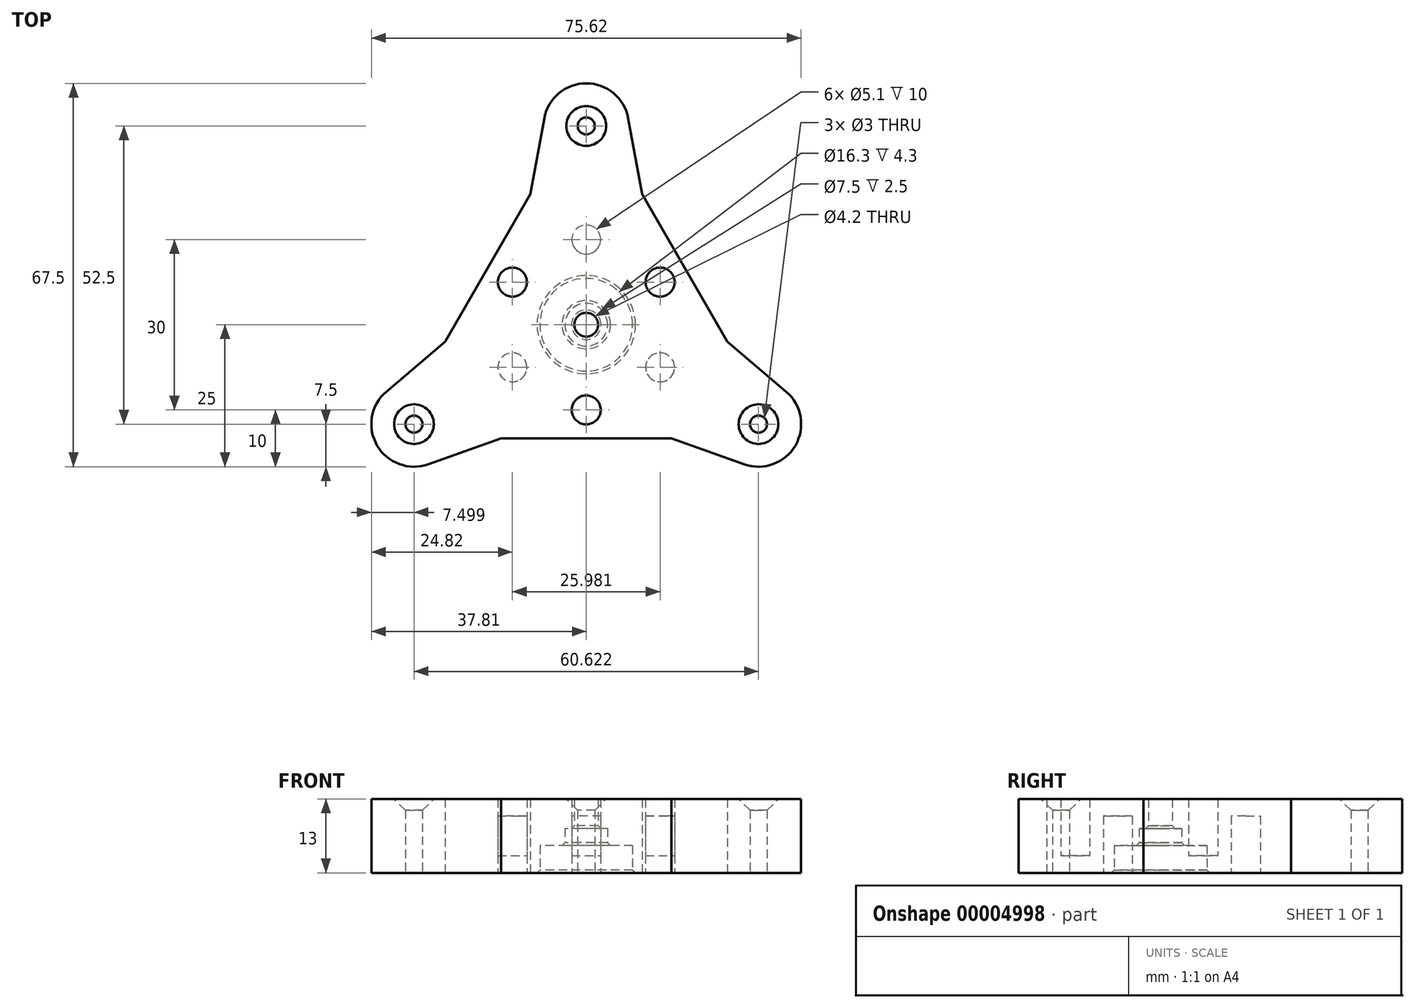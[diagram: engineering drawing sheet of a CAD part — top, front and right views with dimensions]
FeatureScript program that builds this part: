
annotation { "Feature Type Name" : "Feature", "Feature Type Description" : "" }
export const myFeature = defineFeature(function(context is Context, id is Id, definition is map)
    precondition{}
    {
        {
            var Q0;
            Q0=qCreatedBy(makeId("Top.planeOp"),FACE);
            var sketch = newSketch(context, id + "F0", { "sketchPlane" : qUnion([Q0])});
            skCircle(sketch, "E0", {"center": v(0, 0) * mm, "radius": 20 * mm, "construction": true});
            skLineSegment(sketch, "E1", {"start": v(0, 0) * mm, "end": v(0, 35) * mm, "construction": true});
            skCircle(sketch, "E2", {"center": v(0, 35) * mm, "radius": 3 * mm, "construction": true});
            skCircle(sketch, "E3", {"center": v(0, 0) * mm, "radius": 8.15 * mm, "construction": true});
            skCircle(sketch, "E4", {"center": v(0, 0) * mm, "radius": 15 * mm, "construction": true});
            skLineSegment(sketch, "E5", {"start": v(0, 0) * mm, "end": v(-17.32, 10) * mm, "construction": true});
            skLineSegment(sketch, "E6", {"start": v(-17.32, 10) * mm, "end": v(-9.82, 23) * mm});
            skArc(sketch, "E7", {"start": v(-7.38, 36.35) * mm, "mid": v(0, 42.5) * mm, "end": v(7.38, 36.35) * mm});
            skLineSegment(sketch, "E8", {"start": v(-7.38, 36.35) * mm, "end": v(-9.82, 23) * mm});
            skArc(sketch, "E9", {"start": v(-7.06, 4.07) * mm, "mid": v(0, 8.15) * mm, "end": v(7.06, 4.07) * mm});
            skLineSegment(sketch, "E10", {"start": v(-17.32, 10) * mm, "end": v(-7.06, 4.07) * mm});
            skLineSegment(sketch, "E11.MirrorCS", {"start": v(7.38, 36.35) * mm, "end": v(9.82, 23) * mm});
            skLineSegment(sketch, "E12.MirrorCS", {"start": v(17.32, 10) * mm, "end": v(9.82, 23) * mm});
            skLineSegment(sketch, "E13.MirrorCS", {"start": v(17.32, 10) * mm, "end": v(7.06, 4.07) * mm});
            skCircle(sketch, "E14", {"center": v(0, 35) * mm, "radius": 1.5 * mm});
            skSolve(sketch);
        }
        {
            var Q0;
            Q0=qSketchRegion(id+"F0",true);
            extrude(context, id + "F1", {"entities" : qUnion([Q0]), "depth" : 4.8 * mm, "offsetDistance" : 25 * mm});
        }
        {
            var Q0;
            Q0=makeQuery(id+"F1.opExtrude","CAP_FACE",FACE,{"disambiguationData":[OSD([sQuery(id+"F0.wireOp",EDGE,"E6"),sQuery(id+"F0.wireOp",EDGE,"E7"),sQuery(id+"F0.wireOp",EDGE,"E8"),sQuery(id+"F0.wireOp",EDGE,"E9"),sQuery(id+"F0.wireOp",EDGE,"E10"),sQuery(id+"F0.wireOp",EDGE,"E11.MirrorCS"),sQuery(id+"F0.wireOp",EDGE,"E12.MirrorCS"),sQuery(id+"F0.wireOp",EDGE,"E13.MirrorCS"),sQuery(id+"F0.wireOp",EDGE,"E14")])],"isStart":false});
            var sketch = newSketch(context, id + "F2", { "sketchPlane" : qUnion([Q0])});
            skCircle(sketch, "E15", {"center": v(0, 0) * mm, "radius": 3.75 * mm, "construction": true});
            skArc(sketch, "E16", {"start": v(-3.25, 1.87) * mm, "mid": v(0, 3.75) * mm, "end": v(3.25, 1.87) * mm});
            skLineSegment(sketch, "E17", {"start": v(-17.32, 10) * mm, "end": v(-3.25, 1.87) * mm});
            skLineSegment(sketch, "E18", {"start": v(0, 0) * mm, "end": v(0, 35) * mm, "construction": true});
            skLineSegment(sketch, "E19.0", {"start": v(-17.32, 10) * mm, "end": v(-9.82, 23) * mm});
            skLineSegment(sketch, "E19.1", {"start": v(-7.38, 36.35) * mm, "end": v(-9.82, 23) * mm});
            skArc(sketch, "E19.2", {"start": v(-7.38, 36.35) * mm, "mid": v(0, 42.5) * mm, "end": v(7.38, 36.35) * mm});
            skLineSegment(sketch, "E19.3", {"start": v(7.38, 36.35) * mm, "end": v(9.82, 23) * mm});
            skLineSegment(sketch, "E19.4", {"start": v(17.32, 10) * mm, "end": v(9.82, 23) * mm});
            skCircle(sketch, "E20.0", {"center": v(0, 35) * mm, "radius": 1.5 * mm});
            skLineSegment(sketch, "E21.MirrorCS", {"start": v(17.32, 10) * mm, "end": v(3.25, 1.87) * mm});
            skSolve(sketch);
        }
        {
            var Q0;
            Q0=qSketchRegion(id+"F2",true);
            extrude(context, id + "F3", {"entities" : qUnion([Q0]), "operationType" : NewBodyOperationType.ADD, "depth" : 3 * mm, "offsetDistance" : 25 * mm});
        }
        {
            var Q0;
            Q0=makeQuery(id+"F3.opExtrude","CAP_FACE",FACE,{"disambiguationData":[OSD([sQuery(id+"F2.wireOp",EDGE,"E16"),sQuery(id+"F2.wireOp",EDGE,"E17"),sQuery(id+"F2.wireOp",EDGE,"E19.0"),sQuery(id+"F2.wireOp",EDGE,"E19.1"),sQuery(id+"F2.wireOp",EDGE,"E19.2"),sQuery(id+"F2.wireOp",EDGE,"E19.3"),sQuery(id+"F2.wireOp",EDGE,"E19.4"),sQuery(id+"F2.wireOp",EDGE,"E20.0"),sQuery(id+"F2.wireOp",EDGE,"E21.MirrorCS")])],"isStart":false});
            var sketch = newSketch(context, id + "F4", { "sketchPlane" : qUnion([Q0])});
            skCircle(sketch, "E22", {"center": v(0, 0) * mm, "radius": 2.1 * mm, "construction": true});
            skArc(sketch, "E23", {"start": v(-1.82, 1.05) * mm, "mid": v(0, 2.1) * mm, "end": v(1.82, 1.05) * mm});
            skLineSegment(sketch, "E24", {"start": v(0, 0) * mm, "end": v(0, 35) * mm, "construction": true});
            skLineSegment(sketch, "E25", {"start": v(-17.32, 10) * mm, "end": v(-1.82, 1.05) * mm});
            skLineSegment(sketch, "E26.0", {"start": v(-17.32, 10) * mm, "end": v(-9.82, 23) * mm});
            skLineSegment(sketch, "E26.1", {"start": v(-7.38, 36.35) * mm, "end": v(-9.82, 23) * mm});
            skArc(sketch, "E26.2", {"start": v(-7.38, 36.35) * mm, "mid": v(0, 42.5) * mm, "end": v(7.38, 36.35) * mm});
            skCircle(sketch, "E27.0", {"center": v(0, 35) * mm, "radius": 1.5 * mm});
            skLineSegment(sketch, "E28.MirrorCS", {"start": v(17.32, 10) * mm, "end": v(1.82, 1.05) * mm});
            skLineSegment(sketch, "E29.MirrorCS", {"start": v(17.32, 10) * mm, "end": v(9.82, 23) * mm});
            skLineSegment(sketch, "E30.MirrorCS", {"start": v(7.38, 36.35) * mm, "end": v(9.82, 23) * mm});
            skSolve(sketch);
        }
        {
            var Q0;
            Q0=qSketchRegion(id+"F4",true);
            extrude(context, id + "F5", {"entities" : qUnion([Q0]), "operationType" : NewBodyOperationType.ADD, "depth" : 5.2 * mm, "offsetDistance" : 25 * mm});
        }
        {
            var Q0;
            Q0=makeQuery(id+"F1.opExtrude","CAP_FACE",FACE,{"disambiguationData":[OSD([sQuery(id+"F0.wireOp",EDGE,"E6"),sQuery(id+"F0.wireOp",EDGE,"E7"),sQuery(id+"F0.wireOp",EDGE,"E8"),sQuery(id+"F0.wireOp",EDGE,"E9"),sQuery(id+"F0.wireOp",EDGE,"E10"),sQuery(id+"F0.wireOp",EDGE,"E11.MirrorCS"),sQuery(id+"F0.wireOp",EDGE,"E12.MirrorCS"),sQuery(id+"F0.wireOp",EDGE,"E13.MirrorCS"),sQuery(id+"F0.wireOp",EDGE,"E14")])],"isStart":true});
            var sketch = newSketch(context, id + "F6", { "sketchPlane" : qUnion([Q0])});
            skCircle(sketch, "E31", {"center": v(0, 0) * mm, "radius": 15 * mm, "construction": true});
            skCircle(sketch, "E32", {"center": v(-13, -7.5) * mm, "radius": 2.55 * mm});
            skCircle(sketch, "E33", {"center": v(0, -15) * mm, "radius": 2.55 * mm});
            skCircle(sketch, "E34", {"center": v(13, -7.5) * mm, "radius": 2.55 * mm});
            skSolve(sketch);
        }
        {
            var Q0;
            Q0=qSketchRegion(id+"F6",true);
            extrude(context, id + "F7", {"entities" : qUnion([Q0]), "operationType" : NewBodyOperationType.REMOVE, "endBound" : BoundingType.THROUGH_ALL, "oppositeDirection" : true, "depth" : 25 * mm, "offsetDistance" : 25 * mm});
        }
        {
            var Q0;
            Q0=makeQuery(id+"F5.opExtrude","CAP_EDGE",EDGE,{"disambiguationData":[OSD([sQuery(id+"F4.wireOp",EDGE,"E27.0")])],"isStart":false});
            chamfer(context, id + "F8", {"entities" : qUnion([Q0]), "width" : 2 * mm, "tangentPropagation" : true});
        }
        {
            var Q0;
            Q0=makeQuery(id+"F1.opExtrude","SWEPT_BODY",BODY,{"disambiguationData":[OSD([sQuery(id+"F0.wireOp",EDGE,"E6"),sQuery(id+"F0.wireOp",EDGE,"E7"),sQuery(id+"F0.wireOp",EDGE,"E8"),sQuery(id+"F0.wireOp",EDGE,"E9"),sQuery(id+"F0.wireOp",EDGE,"E10"),sQuery(id+"F0.wireOp",EDGE,"E11.MirrorCS"),sQuery(id+"F0.wireOp",EDGE,"E12.MirrorCS"),sQuery(id+"F0.wireOp",EDGE,"E13.MirrorCS"),sQuery(id+"F0.wireOp",EDGE,"E14")])]});
            var Q1;
            Q1=makeQuery(id+"F5.opExtrude","SWEPT_FACE",FACE,{"disambiguationData":[OSD([sQuery(id+"F4.wireOp",EDGE,"E23")])]});
            circularPattern(context, id + "F9", {"entities" : qUnion([Q0]), "axis" : qUnion([Q1]), "angle" : 360 * degree, "instanceCount" : 3, "equalSpace" : true});
        }
        {
            var Q0;
            Q0=makeQuery(id+"F1.opExtrude","SWEPT_BODY",BODY,{"disambiguationData":[OSD([sQuery(id+"F0.wireOp",EDGE,"E6"),sQuery(id+"F0.wireOp",EDGE,"E7"),sQuery(id+"F0.wireOp",EDGE,"E8"),sQuery(id+"F0.wireOp",EDGE,"E9"),sQuery(id+"F0.wireOp",EDGE,"E10"),sQuery(id+"F0.wireOp",EDGE,"E11.MirrorCS"),sQuery(id+"F0.wireOp",EDGE,"E12.MirrorCS"),sQuery(id+"F0.wireOp",EDGE,"E13.MirrorCS"),sQuery(id+"F0.wireOp",EDGE,"E14")])]});
            var Q1;
            Q1=makeQuery(id+"F9.opPattern","COPY",BODY,{"derivedFrom":makeQuery(id+"F1.opExtrude","SWEPT_BODY",BODY,{"disambiguationData":[OSD([sQuery(id+"F0.wireOp",EDGE,"E6"),sQuery(id+"F0.wireOp",EDGE,"E7"),sQuery(id+"F0.wireOp",EDGE,"E8"),sQuery(id+"F0.wireOp",EDGE,"E9"),sQuery(id+"F0.wireOp",EDGE,"E10"),sQuery(id+"F0.wireOp",EDGE,"E11.MirrorCS"),sQuery(id+"F0.wireOp",EDGE,"E12.MirrorCS"),sQuery(id+"F0.wireOp",EDGE,"E13.MirrorCS"),sQuery(id+"F0.wireOp",EDGE,"E14")])]}),"instanceName":"1"});
            var Q2;
            Q2=makeQuery(id+"F9.opPattern","COPY",BODY,{"derivedFrom":makeQuery(id+"F1.opExtrude","SWEPT_BODY",BODY,{"disambiguationData":[OSD([sQuery(id+"F0.wireOp",EDGE,"E6"),sQuery(id+"F0.wireOp",EDGE,"E7"),sQuery(id+"F0.wireOp",EDGE,"E8"),sQuery(id+"F0.wireOp",EDGE,"E9"),sQuery(id+"F0.wireOp",EDGE,"E10"),sQuery(id+"F0.wireOp",EDGE,"E11.MirrorCS"),sQuery(id+"F0.wireOp",EDGE,"E12.MirrorCS"),sQuery(id+"F0.wireOp",EDGE,"E13.MirrorCS"),sQuery(id+"F0.wireOp",EDGE,"E14")])]}),"instanceName":"2"});
            booleanBodies(context, id + "F10", {"operationType" : BooleanOperationType.UNION, "tools" : qUnion([Q0, Q1, Q2])});
        }
        {
            var Q0;
            {var subQ0=makeQuery(id+"F1.opExtrude","CAP_EDGE",EDGE,{"disambiguationData":[OSD([sQuery(id+"F0.wireOp",EDGE,"E9")])],"isStart":true});Q0=makeQuery(id+"F10.opBoolean","MERGE",EDGE,{"derivedFrom":[subQ0,makeQuery(id+"F9.opPattern","COPY",EDGE,{"derivedFrom":subQ0,"instanceName":"1"}),makeQuery(id+"F9.opPattern","COPY",EDGE,{"derivedFrom":subQ0,"instanceName":"2"})]});}
            var Q1;
            {var subQ0=makeQuery(id+"F3.opExtrude","CAP_EDGE",EDGE,{"disambiguationData":[OSD([sQuery(id+"F2.wireOp",EDGE,"E16")])],"isStart":true});Q1=makeQuery(id+"F10.opBoolean","MERGE",EDGE,{"derivedFrom":[subQ0,makeQuery(id+"F9.opPattern","COPY",EDGE,{"derivedFrom":subQ0,"instanceName":"1"}),makeQuery(id+"F9.opPattern","COPY",EDGE,{"derivedFrom":subQ0,"instanceName":"2"})]});}
            var Q2;
            {var subQ0=makeQuery(id+"F5.opExtrude","CAP_EDGE",EDGE,{"disambiguationData":[OSD([sQuery(id+"F4.wireOp",EDGE,"E23")])],"isStart":true});Q2=makeQuery(id+"F10.opBoolean","MERGE",EDGE,{"derivedFrom":[subQ0,makeQuery(id+"F9.opPattern","COPY",EDGE,{"derivedFrom":subQ0,"instanceName":"1"}),makeQuery(id+"F9.opPattern","COPY",EDGE,{"derivedFrom":subQ0,"instanceName":"2"})]});}
            chamfer(context, id + "F11", {"entities" : qUnion([Q0, Q1, Q2]), "width" : .5 * mm, "tangentPropagation" : true});
        }
        {
            var Q0;
            {var subQ0=makeQuery(id+"F5.opExtrude","CAP_FACE",FACE,{"disambiguationData":[OSD([sQuery(id+"F4.wireOp",EDGE,"E23"),sQuery(id+"F4.wireOp",EDGE,"E25"),sQuery(id+"F4.wireOp",EDGE,"E26.0"),sQuery(id+"F4.wireOp",EDGE,"E26.1"),sQuery(id+"F4.wireOp",EDGE,"E26.2"),sQuery(id+"F4.wireOp",EDGE,"E27.0"),sQuery(id+"F4.wireOp",EDGE,"E28.MirrorCS"),sQuery(id+"F4.wireOp",EDGE,"E29.MirrorCS"),sQuery(id+"F4.wireOp",EDGE,"E30.MirrorCS")])],"isStart":false});Q0=makeQuery(id+"FO7N2yduhNKENT9_1.boolean.opBoolean","MERGE",FACE,{"derivedFrom":[makeQuery(id+"F10.opBoolean","MERGE",FACE,{"derivedFrom":[subQ0,makeQuery(id+"F9.opPattern","COPY",FACE,{"derivedFrom":subQ0,"instanceName":"1"}),makeQuery(id+"F9.opPattern","COPY",FACE,{"derivedFrom":subQ0,"instanceName":"2"})]}),makeQuery(id+"FO7N2yduhNKENT9_1.opExtrude","CAP_FACE",FACE,{"disambiguationData":[OSD([sQuery(id+"FNLnepW79swXow8_1.wireOp",EDGE,"SIupkN1O-Omlc-O9Fm-OHPS-0TtmnWLN5T4D"),sQuery(id+"FNLnepW79swXow8_1.wireOp",EDGE,"nX4cWOXq-HYvH-e0Jd-PPum-Qjxn0gHoVHlj"),sQuery(id+"FNLnepW79swXow8_1.wireOp",EDGE,"Kmg2HQq8-LBUH-nA9Y-GviP-fJ5rH8yUH7kr"),sQuery(id+"FNLnepW79swXow8_1.wireOp",EDGE,"dawWJMjc-QiiI-OI5V-u3eX-lsZ4HrKREf6o")])],"isStart":true})]});}
            var sketch = newSketch(context, id + "F12", { "sketchPlane" : qUnion([Q0])});
            skCircle(sketch, "E35.0", {"center": v(13, -7.5) * mm, "radius": 2.55 * mm});
            skCircle(sketch, "E35.1", {"center": v(-13, -7.5) * mm, "radius": 2.55 * mm});
            skCircle(sketch, "E35.2", {"center": v(0, 15) * mm, "radius": 2.55 * mm});
            skSolve(sketch);
        }
        {
            var Q0;
            Q0=qSketchRegion(id+"F12",true);
            extrude(context, id + "F13", {"entities" : qUnion([Q0]), "operationType" : NewBodyOperationType.ADD, "oppositeDirection" : true, "depth" : 3 * mm, "offsetDistance" : 25 * mm});
        }
        {
            var Q0;
            {var subQ0=makeQuery(id+"F1.opExtrude","CAP_FACE",FACE,{"disambiguationData":[OSD([sQuery(id+"F0.wireOp",EDGE,"E6"),sQuery(id+"F0.wireOp",EDGE,"E7"),sQuery(id+"F0.wireOp",EDGE,"E8"),sQuery(id+"F0.wireOp",EDGE,"E9"),sQuery(id+"F0.wireOp",EDGE,"E10"),sQuery(id+"F0.wireOp",EDGE,"E11.MirrorCS"),sQuery(id+"F0.wireOp",EDGE,"E12.MirrorCS"),sQuery(id+"F0.wireOp",EDGE,"E13.MirrorCS"),sQuery(id+"F0.wireOp",EDGE,"E14")])],"isStart":true});Q0=makeQuery(id+"FO7N2yduhNKENT9_1.boolean.opBoolean","MERGE",FACE,{"derivedFrom":[makeQuery(id+"F10.opBoolean","MERGE",FACE,{"derivedFrom":[subQ0,makeQuery(id+"F9.opPattern","COPY",FACE,{"derivedFrom":subQ0,"instanceName":"1"}),makeQuery(id+"F9.opPattern","COPY",FACE,{"derivedFrom":subQ0,"instanceName":"2"})]}),makeQuery(id+"FO7N2yduhNKENT9_1.opExtrude","CAP_FACE",FACE,{"disambiguationData":[OSD([sQuery(id+"FNLnepW79swXow8_1.wireOp",EDGE,"SIupkN1O-Omlc-O9Fm-OHPS-0TtmnWLN5T4D"),sQuery(id+"FNLnepW79swXow8_1.wireOp",EDGE,"nX4cWOXq-HYvH-e0Jd-PPum-Qjxn0gHoVHlj"),sQuery(id+"FNLnepW79swXow8_1.wireOp",EDGE,"Kmg2HQq8-LBUH-nA9Y-GviP-fJ5rH8yUH7kr"),sQuery(id+"FNLnepW79swXow8_1.wireOp",EDGE,"dawWJMjc-QiiI-OI5V-u3eX-lsZ4HrKREf6o")])],"isStart":false})]});}
            var sketch = newSketch(context, id + "F14", { "sketchPlane" : qUnion([Q0])});
            skCircle(sketch, "E36", {"center": v(0, 15) * mm, "radius": 2.55 * mm});
            skCircle(sketch, "E37", {"center": v(-13, -7.5) * mm, "radius": 2.55 * mm});
            skCircle(sketch, "E38", {"center": v(13, -7.5) * mm, "radius": 2.55 * mm});
            skSolve(sketch);
        }
        {
            var Q0;
            Q0=qSketchRegion(id+"F14",true);
            extrude(context, id + "F15", {"entities" : qUnion([Q0]), "operationType" : NewBodyOperationType.ADD, "oppositeDirection" : true, "depth" : 3 * mm, "offsetDistance" : 25 * mm});
        }
    });
